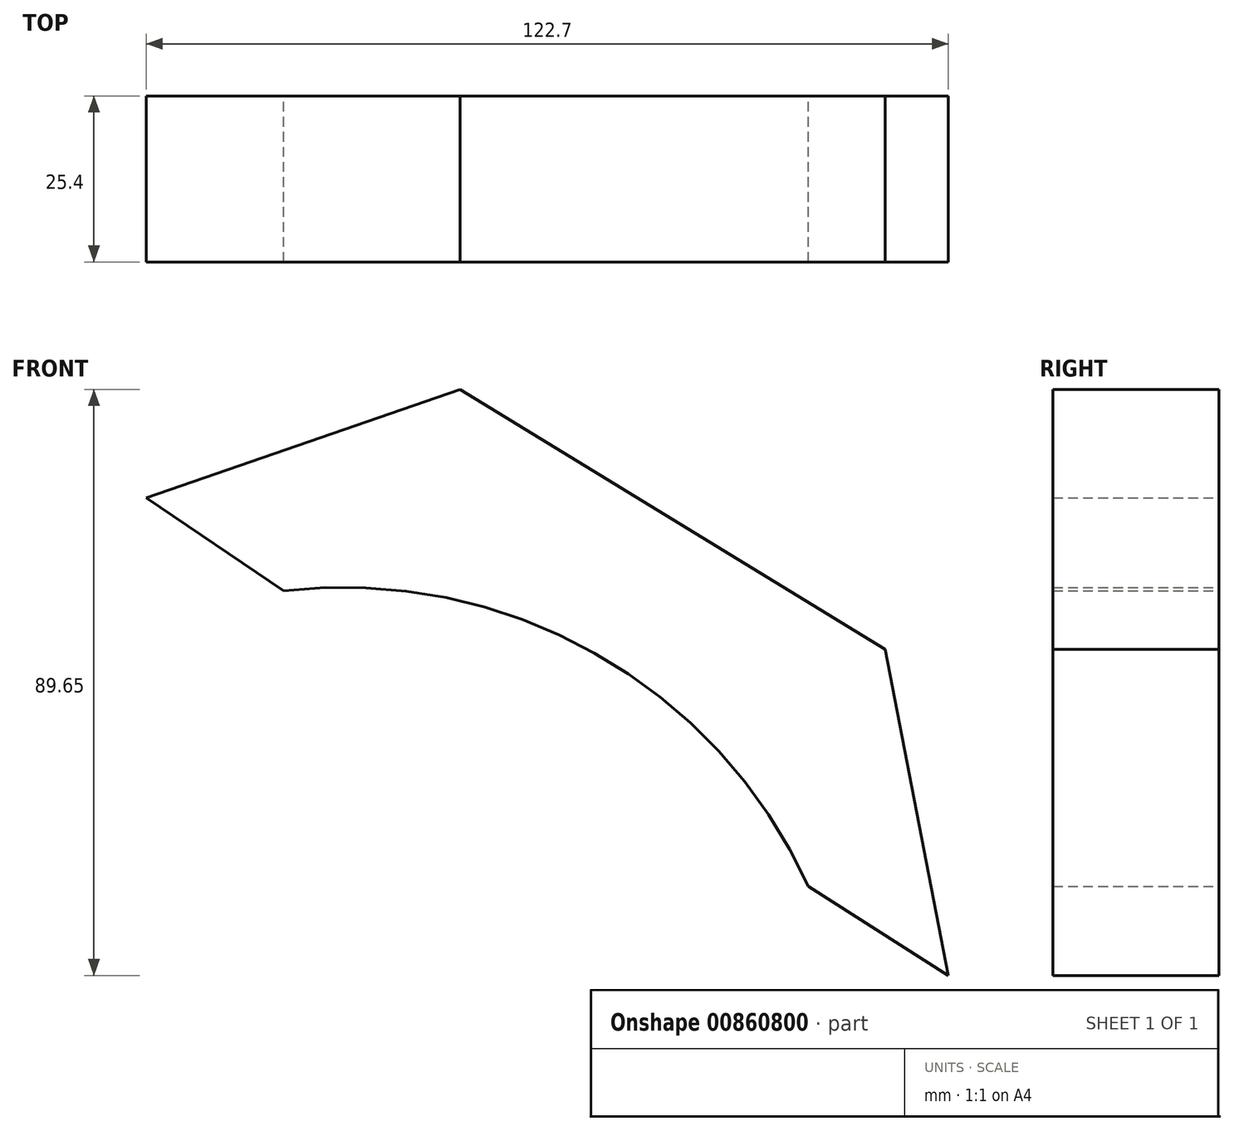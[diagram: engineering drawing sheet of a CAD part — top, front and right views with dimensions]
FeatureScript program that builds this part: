
annotation { "Feature Type Name" : "Feature", "Feature Type Description" : "" }
export const myFeature = defineFeature(function(context is Context, id is Id, definition is map)
    precondition{}
    {
        {
            var Q0;
            Q0=qCreatedBy(makeId("Front.planeOp"),FACE);
            var sketch = newSketch(context, id + "F0", { "sketchPlane" : qUnion([Q0])});
            skLineSegment(sketch, "E0", {"start": v(2.53, -40.31) * mm, "end": v(23.97, -53.93) * mm});
            skLineSegment(sketch, "E1", {"start": v(23.97, -53.93) * mm, "end": v(14.29, -4.06) * mm});
            skLineSegment(sketch, "E2", {"start": v(14.29, -4.06) * mm, "end": v(-50.71, 35.72) * mm});
            skLineSegment(sketch, "E3", {"start": v(-50.71, 35.72) * mm, "end": v(-98.73, 19.14) * mm});
            skLineSegment(sketch, "E4", {"start": v(-98.73, 19.14) * mm, "end": v(-77.7, 4.9) * mm});
            skArc(sketch, "E5", {"start": v(2.53, -40.31) * mm, "mid": v(-30.2, -4.6) * mm, "end": v(-77.7, 4.9) * mm});
            skSolve(sketch);
        }
        {
            var Q0;
            Q0=qSketchRegion(id+"F0",true);
            extrude(context, id + "F1", {"entities" : qUnion([Q0]), "depth" : 25.4 * mm, "offsetDistance" : 25.4 * mm});
        }
    });
